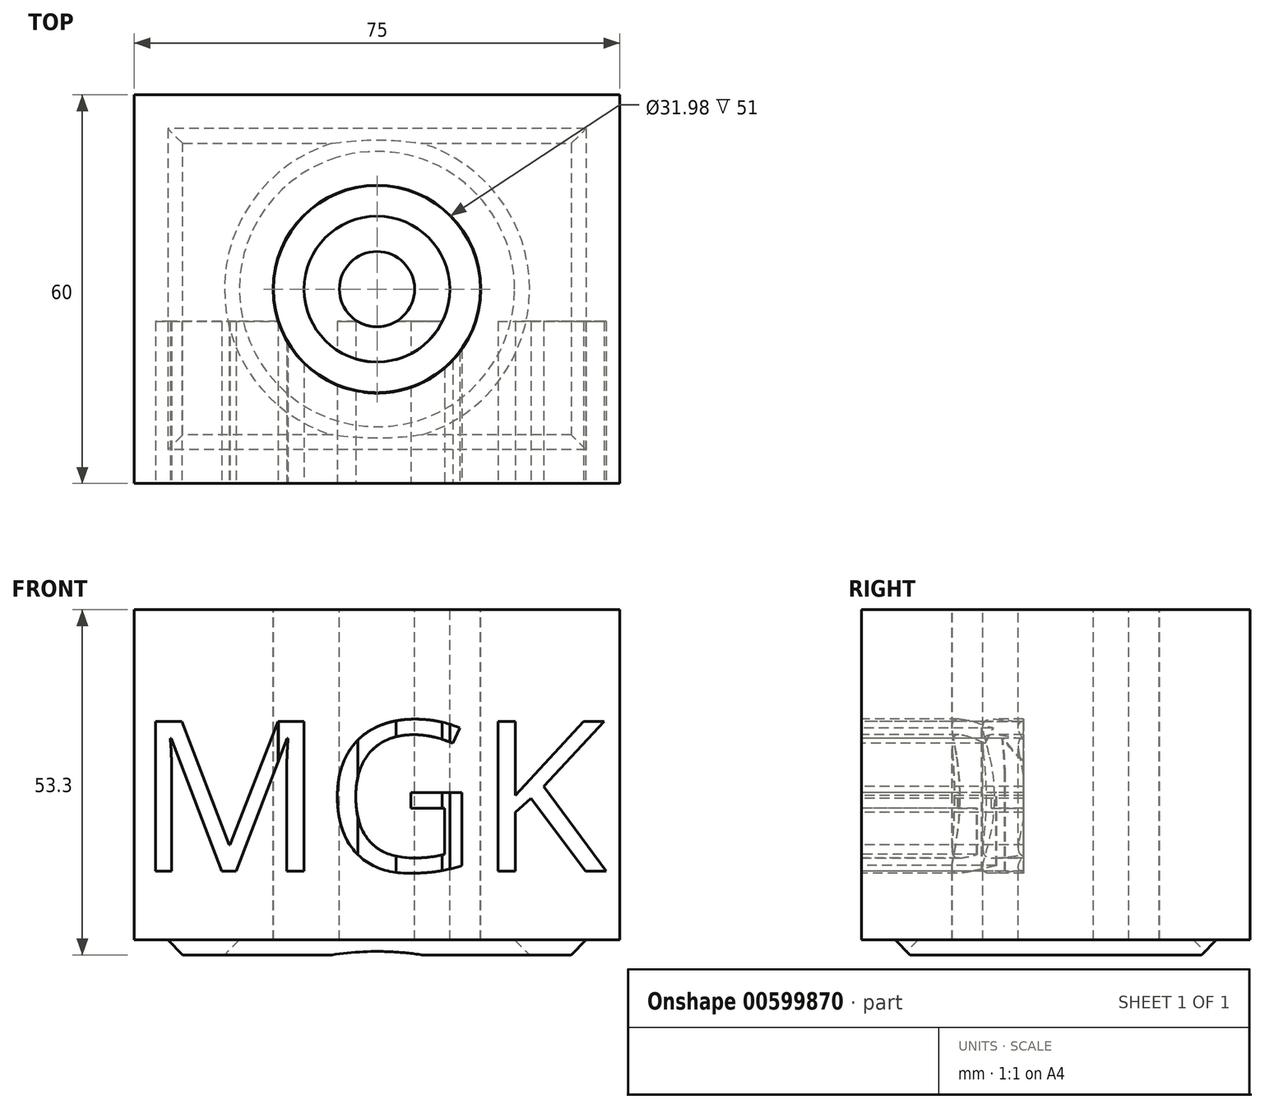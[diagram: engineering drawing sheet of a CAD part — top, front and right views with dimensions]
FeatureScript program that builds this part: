
annotation { "Feature Type Name" : "Feature", "Feature Type Description" : "" }
export const myFeature = defineFeature(function(context is Context, id is Id, definition is map)
    precondition{}
    {
        {
            var Q0;
            Q0=qCreatedBy(makeId("Top.planeOp"),FACE);
            var sketch = newSketch(context, id + "F0", { "sketchPlane" : qUnion([Q0])});
            skLineSegment(sketch, "E0.bottom", {"start": v(37.5, 30) * mm, "end": v(-37.5, 30) * mm});
            skLineSegment(sketch, "E0.top", {"start": v(37.5, -30) * mm, "end": v(-37.5, -30) * mm});
            skLineSegment(sketch, "E0.left", {"start": v(37.5, 30) * mm, "end": v(37.5, -30) * mm});
            skLineSegment(sketch, "E0.right", {"start": v(-37.5, 30) * mm, "end": v(-37.5, -30) * mm});
            skPoint(sketch, "E0.middle", {"position": v(0, 0) * mm});
            skSolve(sketch);
        }
        {
            var Q0;
            Q0=makeQuery(id+"F0.imprint","IMPRINT",FACE,{"disambiguationData":[TD([[makeQuery(id+"F0.imprint","IMPRINT",EDGE,{"derivedFrom":sQuery(id+"F0.wireOp",EDGE,"E0.bottom")}),1.0]])]});
            extrude(context, id + "F1", {"entities" : qUnion([Q0]), "depth" : 51 * mm, "offsetDistance" : 25 * mm});
        }
        {
            var Q0;
            Q0=makeQuery(id+"F1.opExtrude","CAP_FACE",FACE,{"disambiguationData":[OSD([sQuery(id+"F0.wireOp",EDGE,"E0.bottom"),sQuery(id+"F0.wireOp",EDGE,"E0.top"),sQuery(id+"F0.wireOp",EDGE,"E0.left"),sQuery(id+"F0.wireOp",EDGE,"E0.right")])],"isStart":false});
            var sketch = newSketch(context, id + "F2", { "sketchPlane" : qUnion([Q0])});
            skCircle(sketch, "E1", {"center": v(0, 0) * mm, "radius": 16 * mm});
            skCircle(sketch, "E2", {"center": v(0, 0) * mm, "radius": 11.26 * mm});
            skCircle(sketch, "E3", {"center": v(0, 0) * mm, "radius": 5.8 * mm});
            skCircle(sketch, "E4", {"center": v(0, 0) * mm, "radius": 3.26 * mm});
            skCircle(sketch, "E5", {"center": v(0, 0) * mm, "radius": 16.06 * mm});
            skSolve(sketch);
        }
        {
            var Q0;
            Q0 = qSketchRegion(id + "F2", true);
            var Q1;
            Q1=makeQuery(id+"F2.imprint","IMPRINT",FACE,{"disambiguationData":[TD([[makeQuery(id+"F2.imprint","IMPRINT",EDGE,{"derivedFrom":sQuery(id+"F2.wireOp",EDGE,"E1")}),1.0]])]});
            var Q2;
            Q2=makeQuery(id+"F2.imprint","IMPRINT",FACE,{"disambiguationData":[TD([[makeQuery(id+"F2.imprint","IMPRINT",EDGE,{"derivedFrom":sQuery(id+"F2.wireOp",EDGE,"E4")}),1.0]])]});
            var Q3;
            Q3=makeQuery(id+"F2.imprint","IMPRINT",FACE,{"disambiguationData":[TD([[makeQuery(id+"F2.imprint","IMPRINT",EDGE,{"derivedFrom":sQuery(id+"F2.wireOp",EDGE,"E3")}),1.0]])]});
            extrude(context, id + "F3", {"entities" : qUnion([Q0, Q1, Q2, Q3]), "operationType" : NewBodyOperationType.REMOVE, "oppositeDirection" : true, "depth" : 99999 * mm, "offsetDistance" : 25 * mm});
        }
        {
            var Q0;
            {var subQ0=sQuery(id+"F0.wireOp",EDGE,"E0.left");var subQ1=sQuery(id+"F0.wireOp",EDGE,"E0.top");var subQ2=sQuery(id+"F0.wireOp",EDGE,"E0.right");var subQ3=sQuery(id+"F0.wireOp",EDGE,"E0.bottom");Q0=makeQuery(id+"F3.boolean.opBoolean","SPLIT",FACE,{"disambiguationData":[TD([makeQuery(id+"F1.opExtrude","SWEPT_FACE",FACE,{"disambiguationData":[OSD([subQ3])]})])],"derivedFrom":makeQuery(id+"F1.opExtrude","CAP_FACE",FACE,{"disambiguationData":[OSD([subQ3,subQ1,subQ0,subQ2])],"isStart":true})});}
            shell(context, id + "F4", {"entities" : qUnion([Q0]), "thickness" : 2.5 * mm});
        }
        {
            var Q0;
            {var subQ0=sQuery(id+"F0.wireOp",EDGE,"E0.left");var subQ1=sQuery(id+"F0.wireOp",EDGE,"E0.top");var subQ2=sQuery(id+"F0.wireOp",EDGE,"E0.right");var subQ3=sQuery(id+"F0.wireOp",EDGE,"E0.bottom");Q0=makeQuery(id+"F4.opShell","OFFSET_FACE",FACE,{"disambiguationData":[OSD([subQ3,subQ1,subQ0,subQ2]),TDD([makeQuery(id+"F3.boolean.opBoolean","SPLIT",FACE,{"disambiguationData":[TD([makeQuery(id+"F1.opExtrude","SWEPT_FACE",FACE,{"disambiguationData":[OSD([subQ3])]})])],"derivedFrom":makeQuery(id+"F1.opExtrude","CAP_FACE",FACE,{"disambiguationData":[OSD([subQ3,subQ1,subQ0,subQ2])],"isStart":false})})])]});}
            extrude(context, id + "F5", {"entities" : qUnion([Q0]), "operationType" : NewBodyOperationType.ADD, "depth" : 50.8 * mm, "offsetDistance" : 25 * mm});
        }
        {
            var Q0;
            Q0=makeQuery(id+"F5.opExtrude","CAP_FACE",FACE,{"disambiguationData":[OSD([sQuery(id+"F0.wireOp",EDGE,"E0.bottom"),sQuery(id+"F0.wireOp",EDGE,"E0.top"),sQuery(id+"F0.wireOp",EDGE,"E0.left"),sQuery(id+"F0.wireOp",EDGE,"E0.right")])],"isStart":false});
            chamfer(context, id + "F6", {"entities" : qUnion([Q0]), "width" : 5 * mm, "tangentPropagation" : true});
        }
        {
            var Q0;
            Q0=makeQuery(id+"F1.opExtrude","SWEPT_FACE",FACE,{"disambiguationData":[OSD([sQuery(id+"F0.wireOp",EDGE,"E0.top")])]});
            var sketch = newSketch(context, id + "F7", { "sketchPlane" : qUnion([Q0])});
            skText(sketch, "E6", { "text": "MGK", "fontName": "OpenSans-Regular.ttf"});
            const initialGuessF7  = {"E6": [-0.03738, 0.01062, 1, 0, 0.02335]};
            skSetInitialGuess(sketch, initialGuessF7);
            skSolve(sketch);
        }
        {
            var Q0;
            Q0 = qSketchRegion(id + "F7", true);
            extrude(context, id + "F8", {"entities" : qUnion([Q0]), "operationType" : NewBodyOperationType.REMOVE, "oppositeDirection" : true, "depth" : 25 * mm, "offsetDistance" : 25 * mm});
        }
    });
